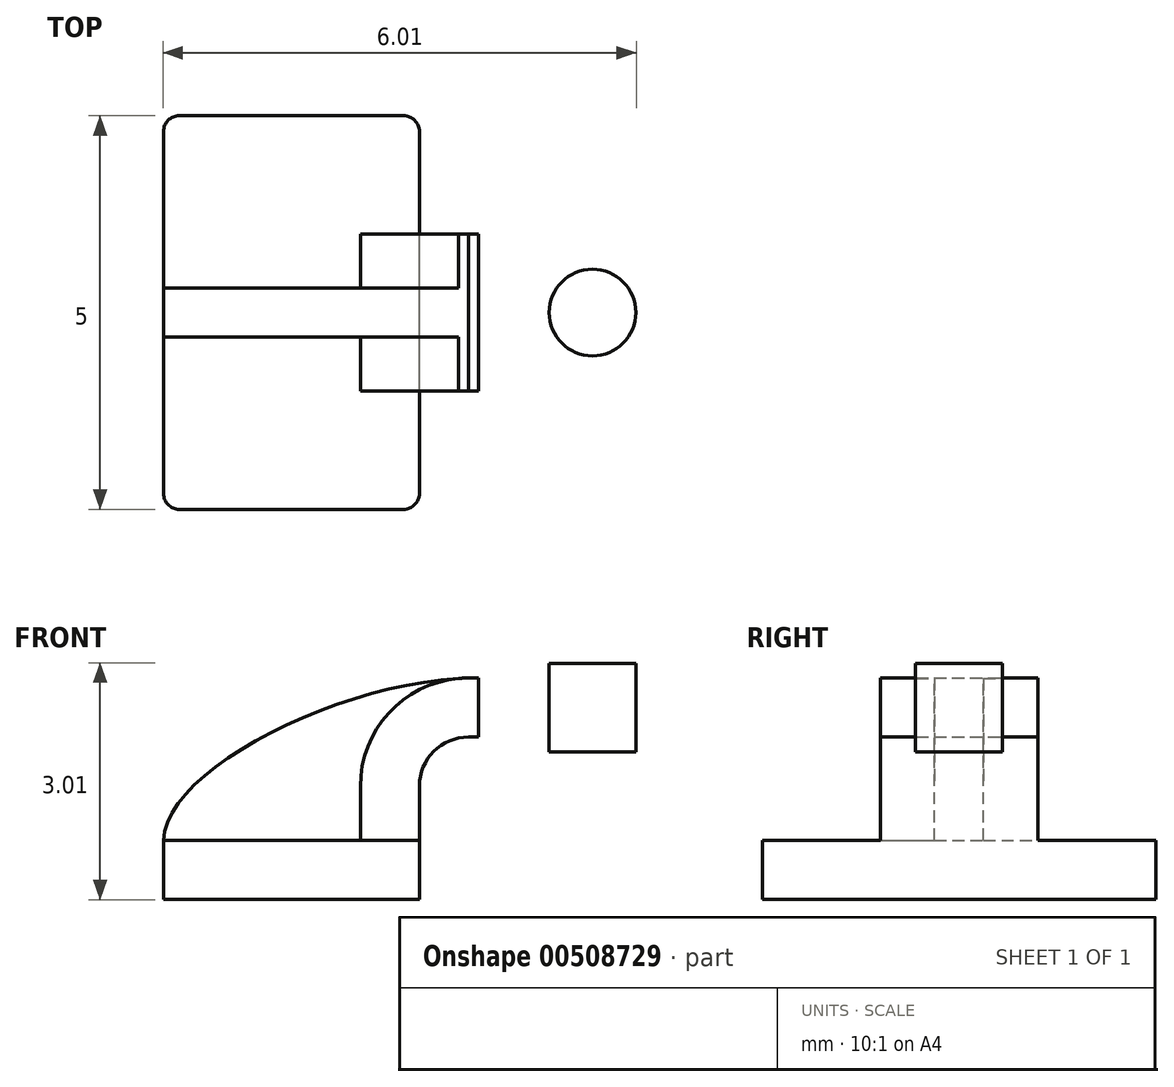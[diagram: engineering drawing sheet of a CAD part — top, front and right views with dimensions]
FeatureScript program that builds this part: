
annotation { "Feature Type Name" : "Feature", "Feature Type Description" : "" }
export const myFeature = defineFeature(function(context is Context, id is Id, definition is map)
    precondition{}
    {
        {
            var Q0;
            Q0=qCreatedBy(makeId("Front.planeOp"),FACE);
            var sketch = newSketch(context, id + "F0", { "sketchPlane" : qUnion([Q0])});
            skLineSegment(sketch, "E0.bottom", {"start": v(1.63, -0.37) * mm, "end": v(-1.63, -0.38) * mm});
            skLineSegment(sketch, "E0.top", {"start": v(1.63, 0.38) * mm, "end": v(-1.63, 0.38) * mm});
            skLineSegment(sketch, "E0.left", {"start": v(1.63, -0.37) * mm, "end": v(1.63, 0.38) * mm});
            skLineSegment(sketch, "E0.right", {"start": v(-1.63, -0.38) * mm, "end": v(-1.63, 0.38) * mm});
            skPoint(sketch, "E0.middle", {"position": v(0, 0) * mm});
            skLineSegment(sketch, "E1.bottom", {"start": v(4.37, 1.5) * mm, "end": v(2.37, 1.5) * mm});
            skLineSegment(sketch, "E1.top", {"start": v(4.38, 2.63) * mm, "end": v(2.37, 2.63) * mm});
            skLineSegment(sketch, "E1.left", {"start": v(4.37, 1.5) * mm, "end": v(4.37, 2.63) * mm});
            skLineSegment(sketch, "E1.right", {"start": v(2.37, 1.5) * mm, "end": v(2.37, 2.62) * mm});
            skPoint(sketch, "E1.middle", {"position": v(3.38, 2.06) * mm});
            skLineSegment(sketch, "E2", {"start": v(1.63, 0.38) * mm, "end": v(1.63, 1.06) * mm});
            skArc(sketch, "E3", {"start": v(1.62, 1.06) * mm, "mid": v(1.8, 1.5) * mm, "end": v(2.25, 1.69) * mm});
            skLineSegment(sketch, "E4", {"start": v(2.25, 1.69) * mm, "end": v(3.82, 1.69) * mm});
            skLineSegment(sketch, "E5.0", {"start": v(2.25, 2.44) * mm, "end": v(3.82, 2.44) * mm});
            skArc(sketch, "E5.1", {"start": v(0.87, 1.06) * mm, "mid": v(1.28, 2.04) * mm, "end": v(2.25, 2.44) * mm});
            skLineSegment(sketch, "E5.2", {"start": v(0.87, 0.38) * mm, "end": v(0.87, 1.06) * mm});
            skFitSpline(sketch, "E6", {"points": [v(-1.63, 0.37) * mm, v(2.25, 2.44) * mm], "startDerivative": vector(0.04, 2.67) * mm, "endDerivative": vector(4.95, 0.15) * mm});
            skLineSegment(sketch, "E7", {"start": v(3.82, 1.5) * mm, "end": v(3.82, 2.63) * mm});
            skLineSegment(sketch, "E8", {"start": v(2.37, 2.44) * mm, "end": v(2.37, 1.69) * mm});
            skLineSegment(sketch, "E9.bottom", {"start": v(2.37, 2.44) * mm, "end": v(3.82, 2.44) * mm});
            skLineSegment(sketch, "E9.top", {"start": v(2.37, 1.69) * mm, "end": v(3.82, 1.69) * mm});
            skLineSegment(sketch, "E9.right", {"start": v(3.82, 2.44) * mm, "end": v(3.82, 1.69) * mm});
            skSolve(sketch);
        }
        {
            var Q0;
            Q0=makeQuery(id+"F0.imprint","IMPRINT",FACE,{"disambiguationData":[TD([[makeQuery(id+"F0.imprint","IMPRINT",EDGE,{"derivedFrom":sQuery(id+"F0.wireOp",EDGE,"E0.bottom")}),-1.0]])]});
            extrude(context, id + "F1", {"entities" : qUnion([Q0]), "endBound" : BoundingType.SYMMETRIC, "depth" : 5 * mm});
        }
        {
            var Q0;
            {var subQ0=sQuery(id+"F0.wireOp",EDGE,"E2");Q0=makeQuery(id+"F0.imprint","IMPRINT",FACE,{"disambiguationData":[TD([[makeQuery(id+"F0.imprint","IMPRINT",EDGE,{"derivedFrom":subQ0}),1.0]])]});}
            var Q1;
            Q1=makeQuery(id+"F0.imprint","IMPRINT",FACE,{"disambiguationData":[TD([[makeQuery(id+"F0.imprint","IMPRINT",EDGE,{"derivedFrom":sQuery(id+"F0.wireOp",EDGE,"E9.bottom")}),-1.0]])]});
            extrude(context, id + "F2", {"entities" : qUnion([Q0, Q1]), "operationType" : NewBodyOperationType.ADD, "endBound" : BoundingType.SYMMETRIC, "depth" : 2 * mm});
        }
        {
            var Q0;
            {var subQ3=sQuery(id+"F0.wireOp",EDGE,"E5.2");Q0=makeQuery(id+"F0.imprint","IMPRINT",FACE,{"disambiguationData":[TD([[makeQuery(id+"F0.imprint","IMPRINT",EDGE,{"derivedFrom":subQ3}),1.0]])]});}
            extrude(context, id + "F3", {"entities" : qUnion([Q0]), "operationType" : NewBodyOperationType.ADD, "endBound" : BoundingType.SYMMETRIC, "depth" : .625 * mm});
        }
        {
            var Q0;
            {var subQ0=sQuery(id+"F0.wireOp",EDGE,"E1.left");Q0=makeQuery(id+"F0.imprint","IMPRINT",FACE,{"disambiguationData":[TD([[makeQuery(id+"F0.imprint","IMPRINT",EDGE,{"derivedFrom":subQ0}),1.0]])]});}
            var Q1;
            Q1=sQuery(id+"F0.wireOp",EDGE,"E7");
            revolve(context, id + "F4", {"operationType" : NewBodyOperationType.ADD, "entities" : qUnion([Q0]), "axis" : qUnion([Q1]), "revolveType" : RevolveType.FULL});
        }
        {
            var Q0;
            Q0=makeQuery(id+"F1.opExtrude","CAP_EDGE",EDGE,{"disambiguationData":[OSD([sQuery(id+"F0.wireOp",EDGE,"E0.right")])],"isStart":false});
            var Q1;
            Q1=makeQuery(id+"F1.opExtrude","CAP_EDGE",EDGE,{"disambiguationData":[OSD([sQuery(id+"F0.wireOp",EDGE,"E0.left")])],"isStart":false});
            var Q2;
            Q2=makeQuery(id+"F1.opExtrude","CAP_EDGE",EDGE,{"disambiguationData":[OSD([sQuery(id+"F0.wireOp",EDGE,"E0.left")])],"isStart":true});
            var Q3;
            Q3=makeQuery(id+"F1.opExtrude","CAP_EDGE",EDGE,{"disambiguationData":[OSD([sQuery(id+"F0.wireOp",EDGE,"E0.right")])],"isStart":true});
            fillet(context, id + "F5", {"entities" : qUnion([Q0, Q1, Q2, Q3]), "radius" : 0.2 * mm, "tangentPropagation" : true, "allowEdgeOverflow" : false});
        }
    });
